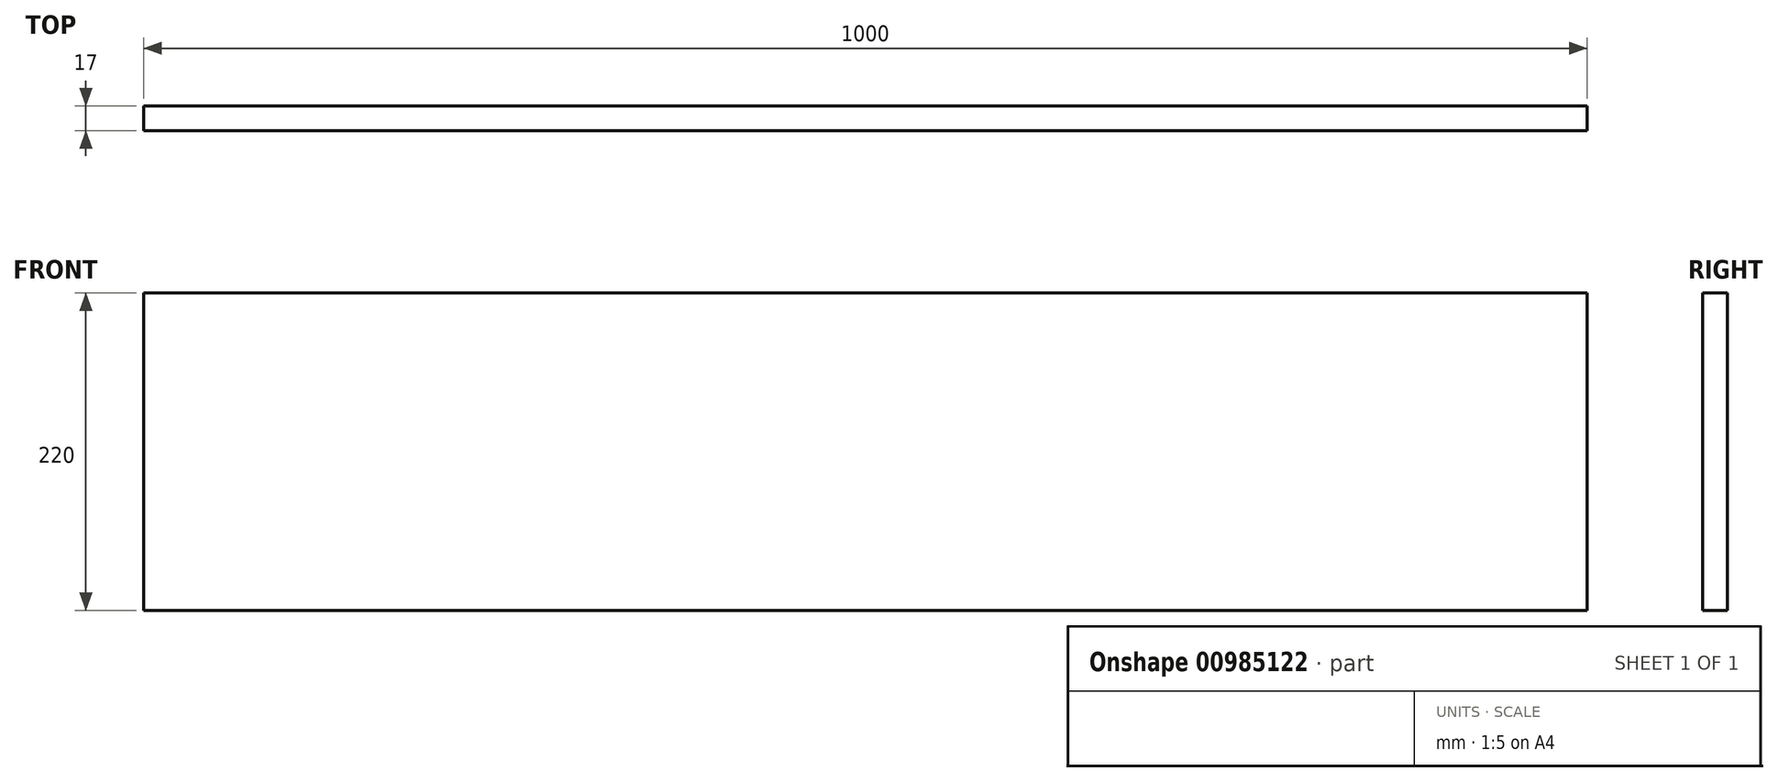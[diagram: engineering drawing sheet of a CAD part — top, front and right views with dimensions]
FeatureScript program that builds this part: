
annotation { "Feature Type Name" : "Feature", "Feature Type Description" : "" }
export const myFeature = defineFeature(function(context is Context, id is Id, definition is map)
    precondition{}
    {
        {
            var Q0;
            Q0=qCreatedBy(makeId("Front.planeOp"),FACE);
            var sketch = newSketch(context, id + "F0", { "sketchPlane" : qUnion([Q0])});
            skLineSegment(sketch, "E0.bottom", {"start": v(-511.19, 58) * mm, "end": v(488.81, 58) * mm});
            skLineSegment(sketch, "E0.top", {"start": v(-511.19, -162) * mm, "end": v(488.81, -162) * mm});
            skLineSegment(sketch, "E0.left", {"start": v(-511.19, 58) * mm, "end": v(-511.19, -162) * mm});
            skLineSegment(sketch, "E0.right", {"start": v(488.81, 58) * mm, "end": v(488.81, -162) * mm});
            skSolve(sketch);
        }
        {
            var Q0;
            Q0 = qSketchRegion(id + "F0", true);
            extrude(context, id + "F1", {"entities" : qUnion([Q0]), "depth" : 17 * mm, "offsetDistance" : 25 * mm});
        }
    });
